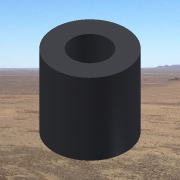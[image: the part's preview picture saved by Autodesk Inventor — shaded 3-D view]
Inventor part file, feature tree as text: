
AUTODESK INVENTOR PART (.ipt)
format: ipt  version: 2014 SP1 (Build 180222100, 222)  size: 123,904 bytes
history: native  units: in
note: dims shown in document units (in); Inventor stores cm internally (conversion verified against a paired STEP export)
features: extrude x1, sketch x1
ambient origin geometry x8: Origin, YZ Plane, XZ Plane, XY Plane, X Axis, Y Axis, Z Axis, Center Point
bodies: Solid1 (feature_tree)
feature tree (2):
  extrude  "Extrusion1"  Depth=2.0in
  sketch  "Sketch1"  dims[d0=8.0in d1=2.0in d2=8.0in d3=0.0in]
